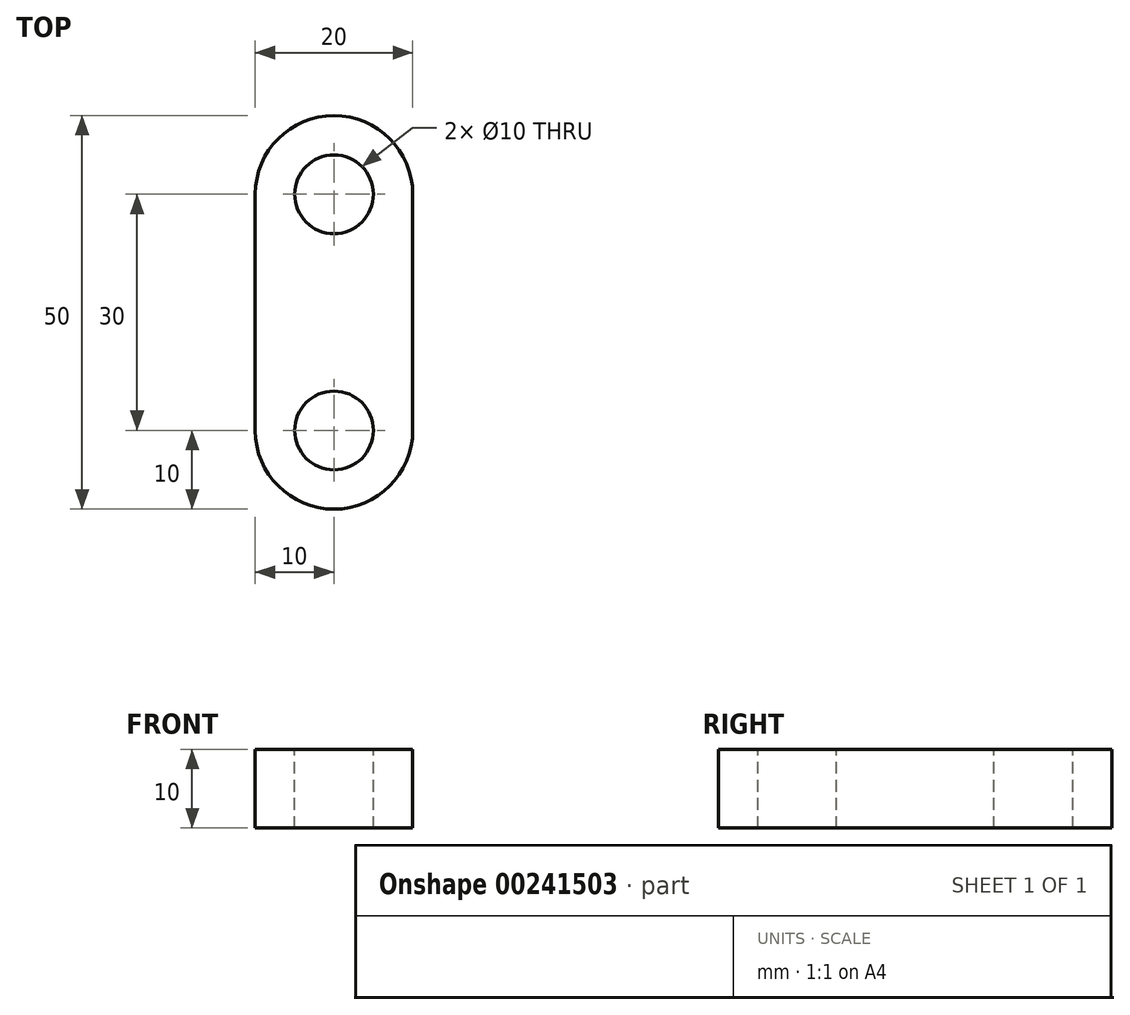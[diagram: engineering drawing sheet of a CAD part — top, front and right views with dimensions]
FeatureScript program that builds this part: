
annotation { "Feature Type Name" : "Feature", "Feature Type Description" : "" }
export const myFeature = defineFeature(function(context is Context, id is Id, definition is map)
    precondition{}
    {
        {
            var Q0;
            Q0=qCreatedBy(makeId("Top.planeOp"),FACE);
            var sketch = newSketch(context, id + "F0", { "sketchPlane" : qUnion([Q0])});
            skArc(sketch, "E0", {"start": v(10, 0) * mm, "mid": v(0, 10) * mm, "end": v(-10, 0) * mm});
            skLineSegment(sketch, "E1", {"start": v(-10, 0) * mm, "end": v(-10, -30) * mm});
            skLineSegment(sketch, "E2", {"start": v(10, 0) * mm, "end": v(10, -30) * mm});
            skArc(sketch, "E3", {"start": v(-10, -30) * mm, "mid": v(0, -40) * mm, "end": v(10, -30) * mm});
            skSolve(sketch);
        }
        {
            var Q0;
            Q0 = qSketchRegion(id + "F0", true);
            extrude(context, id + "F1", {"entities" : qUnion([Q0]), "depth" : 10 * mm});
        }
        {
            var Q0;
            Q0=makeQuery(id+"F1.opExtrude","CAP_FACE",FACE,{"disambiguationData":[OSD([sQuery(id+"F0.wireOp",EDGE,"E0"),sQuery(id+"F0.wireOp",EDGE,"E1"),sQuery(id+"F0.wireOp",EDGE,"E2"),sQuery(id+"F0.wireOp",EDGE,"E3")])],"isStart":false});
            var sketch = newSketch(context, id + "F2", { "sketchPlane" : qUnion([Q0])});
            skPoint(sketch, "E4", {"position": v(0, 0) * mm});
            skPoint(sketch, "E5", {"position": v(0, -30) * mm});
            skSolve(sketch);
        }
        {
            var Q0;
            Q0=sQuery(id+"F2.wireOp",VERTEX,"E4");
            var Q1;
            Q1=sQuery(id+"F2.wireOp",VERTEX,"E5");
            var Q2;
            Q2=makeQuery(id+"F1.opExtrude","SWEPT_BODY",BODY,{"disambiguationData":[OSD([sQuery(id+"F0.wireOp",EDGE,"E0"),sQuery(id+"F0.wireOp",EDGE,"E1"),sQuery(id+"F0.wireOp",EDGE,"E2"),sQuery(id+"F0.wireOp",EDGE,"E3")])]});
            hole(context, id + "F3", {"style" : HoleStyle.SIMPLE, "endStyle" : HoleEndStyle.THROUGH, "holeDiameter" : 10 * mm, "startFromSketch" : true, "locations" : qUnion([Q0, Q1]), "scope" : qUnion([Q2]), "isTappedThrough" : true});
        }
    });
